# Revit family: Splicing cassettes
name_source: partatom
category: Installations électriques
units: mm (PartAtom-declared; Revit-internal decimal feet)

## family parameters
Basée sur le plan de construction = Non
Conserver l'orientation des annotations = Non
Cote de connecteur circulaire = Utiliser le diamètre
Couper avec des vides une fois chargée = Non
Partagée = Non
Point de calcul de pièce = Non
Toujours verticalement = Oui
Type d'élément = Normal

## types (8) — shared parameters
Color = IDS_NOIR
Crossed = Non
Depth = 185 mm  [stored 0.606955 ft]
E-catalogue link = https://www.legrand.fr
ETIM class = EC002699
Function = Pre-equipped cassettes
Height = 43.7 mm  [stored 0.143373 ft]
Operating temperature = -10°C à 60°C
Storage temperature = -10°C à 60°C
Type of connector interior = Other
Width (mm) = 110 mm  [stored 0.360892 ft]
zero-valued in all types: Elévation par défaut, Number of connectors rear side

## per-type parameters (varying)
| type | EAN | Fiber optic class | LC connectors | LC connectors visibility | Legrand part number | Number of connectors front side | SC connectors | SC connectors visibility | Type of connector external |
| Pre-equipped cassette SC duplex 6 fibers multimode | 3414971400337 | OM4 | Splicing LC connectors : LC block 6 fibers multimode | Non | 032180 | 6 | Splicing SC connectors : SC block 6 fibers multimode | Oui | SC_DUPLEX |
| Pre-equipped cassette LC duplex 6 fibers multimode | 3414971400351 | OM4 | Splicing LC connectors : LC block 6 fibers multimode | Oui | 032181 | 6 | Splicing SC connectors : SC block 6 fibers singlemode | Non | LC_DUPLEX |
| Pre-equipped cassette SC duplex 12 fibers multimode | 3414971400375 | OM4 | Splicing LC connectors : LC block 6 fibers singlemode | Non | 032182 | 12 | Splicing SC connectors : SC block 12 fibers multimode | Oui | SC_DUPLEX |
| Pre-equipped cassette LC duplex 12 fibers multimode | 3414971400399 | OM4 | Splicing LC connectors : LC block 12 fibers multimode | Oui | 032183 | 12 | Splicing SC connectors : SC block 6 fibers singlemode | Non | LC_DUPLEX |
| Pre-equipped cassette SC duplex 6 fibers singlemode | 3414971400412 | OS2 | Splicing LC connectors : LC block 6 fibers singlemode | Non | 032184 | 6 | Splicing SC connectors : SC block 6 fibers singlemode | Oui | SC_DUPLEX |
| Pre-equipped cassette LC duplex 6 fibers singlemode | 3414971400436 | OS2 | Splicing LC connectors : LC block 6 fibers singlemode | Oui | 032185 | 6 | Splicing SC connectors : SC block 6 fibers singlemode | Non | LC_DUPLEX |
| Pre-equipped cassette SC duplex 12 fibers singlemode | 3414971400450 | OS2 | Splicing LC connectors : LC block 6 fibers singlemode | Non | 032186 | 12 | Splicing SC connectors : SC block 12 fibers singlemode | Oui | SC_DUPLEX |
| Pre-equipped cassette LC duplex 12 fibers singlemode | 3414971400474 | OS2 | Splicing LC connectors : LC block 12 fibers singlemode | Oui | 032187 | 12 | Splicing SC connectors : SC block 6 fibers singlemode | Non | LC_DUPLEX |

note: column(s) folded — value = type name in every type: BIM wording

note: [stored X ft] marks values corroborated as IEEE doubles in the binary element streams (Revit-internal decimal feet)
